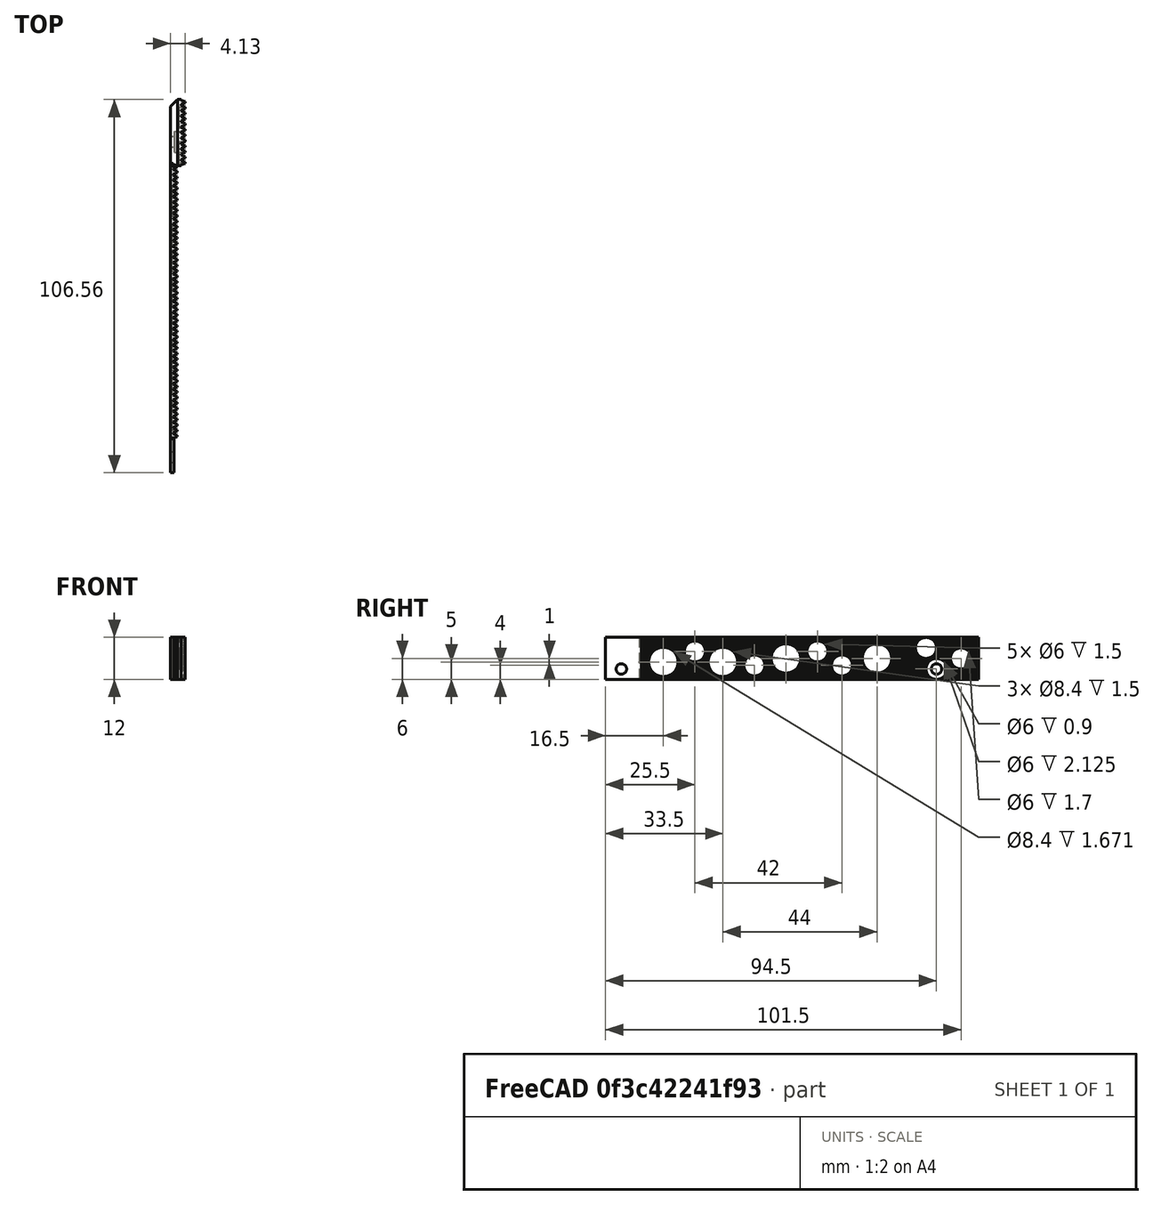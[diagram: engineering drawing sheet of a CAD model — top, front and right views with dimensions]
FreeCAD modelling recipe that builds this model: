
FCSTD DOCUMENT  (FreeCAD 0.19R24276 (Git))
Label: Grip_zubacka_005
License: All rights reserved
LicenseURL: http://en.wikipedia.org/wiki/All_rights_reserved
objects: Part::Cylinder×28, Part::Compound×7, Part::Cut×6, Part::Box×4, Part::FeaturePython×2, Part::Chamfer×1
note: 48 computed .brp shape members not serialized (recipe doc carries the construction recipe); baked Part::Feature solids carry a one-line shape summary decoded from their .brp

FEATURE [Part::FeaturePython] involuterack002  # WARN: FeaturePython — macro-defined, semantics opaque (R4)
  AttacherType = Attacher::AttachEngine3D
  Placement = pos=(23,6,-2) rot=(0,0,1;0rad)
  add_endings = true
  beta = 0
  clearance = 0.25
  double_helix = false
  head = 0
  height = 12
  module = 0.5
  pressure_angle = 20
  properties_from_tool = true
  simplified = false
  teeth = 50
  thickness = 0.8
  transverse_pitch = 1.5708
  version = 0.0.3
FEATURE [Part::FeaturePython] involuterack003  # WARN: FeaturePython — macro-defined, semantics opaque (R4)
  AttacherType = Attacher::AttachEngine3D
  Placement = pos=(25,81,-2) rot=(0,0,1;0rad)
  add_endings = true
  beta = 0
  clearance = 0.25
  double_helix = false
  head = 0
  height = 12
  module = 0.5
  pressure_angle = 20
  properties_from_tool = true
  simplified = false
  teeth = 12
  thickness = 1
  transverse_pitch = 1.5708
  version = 0.0.3
FEATURE [Part::Cylinder] Cylinder3127  label="Válec3097"
  Angle = 360
  AttacherType = Attacher::AttachEngine3D
  Height = 4
  Placement = pos=(1,14,-0.1) rot=(0,0,1;0rad)
  Radius = 1.5
FEATURE [Part::Box] Box1136  label="Krychle1135"
  AttacherType = Attacher::AttachEngine3D
  Height = 12
  Length = 1
  Placement = pos=(21.4,-4.5,-2) rot=(0,0,1;0rad)
  Width = 10
FEATURE [Part::Box] Box1133  label="Krychle1132"
  AttacherType = Attacher::AttachEngine3D
  Height = 2
  Length = 6
  Placement = pos=(-2,11,4) rot=(0,0,1;0rad)
  Width = 6
FEATURE [Part::Cylinder] Cylinder3125  label="Válec3095"
  Angle = 360
  AttacherType = Attacher::AttachEngine3D
  Height = 12
  Placement = pos=(1,14,6) rot=(0,0,1;0rad)
  Radius = 1.5
FEATURE [Part::Cylinder] Cylinder3128  label="Válec3098"
  Angle = 360
  AttacherType = Attacher::AttachEngine3D
  Height = 3
  Placement = pos=(1,14,6) rot=(0,0,1;0rad)
  Radius = 3
FEATURE [Part::Compound] Compound1376
  Links = -> [Cylinder3128]
  Placement = pos=(16.5,73,2) rot=(0,1,0;1.5708rad)
FEATURE [Part::Cut] Cut1266
  Base = -> involuterack003
  Placement = pos=(0.2,3,0) rot=(0,0,1;0rad)
  Tool = -> Compound1376
FEATURE [Part::Box] Box1134  label="Krychle1133"
  AttacherType = Attacher::AttachEngine3D
  Height = 12
  Length = 2
  Placement = pos=(21.4,80,-2) rot=(0,0,1;0rad)
  Width = 19
FEATURE [Part::Cylinder] Cylinder3123  label="Válec3093"
  Angle = 360
  AttacherType = Attacher::AttachEngine3D
  Height = 12
  Placement = pos=(1,14,6) rot=(0,0,1;0rad)
  Radius = 1.5
FEATURE [Part::Cylinder] Cylinder3124  label="Válec3094"
  Angle = 360
  AttacherType = Attacher::AttachEngine3D
  Height = 3
  Placement = pos=(1,14,6) rot=(0,0,1;0rad)
  Radius = 3
FEATURE [Part::Compound] Compound1375
  Links = -> [Cylinder3124]
  Placement = pos=(16.5,73,2) rot=(0,1,0;1.5708rad)
FEATURE [Part::Cylinder] Cylinder3126  label="Válec3096"
  Angle = 360
  AttacherType = Attacher::AttachEngine3D
  Height = 4
  Placement = pos=(1,14,-0.1) rot=(0,0,1;0rad)
  Radius = 1.5
FEATURE [Part::Compound] Compound1373
  Links = -> [Box1133,Cylinder3123,Cylinder3126]
  Placement = pos=(6,73,2) rot=(0,1,0;1.5708rad)
FEATURE [Part::Box] Box1135  label="Krychle1134"
  AttacherType = Attacher::AttachEngine3D
  Height = 2
  Length = 6
  Placement = pos=(-2,11,4) rot=(0,0,1;0rad)
  Width = 6
FEATURE [Part::Compound] Compound1374
  Links = -> [Box1135,Cylinder3125,Cylinder3127]
  Placement = pos=(6,-14,2) rot=(0,1,0;1.5708rad)
FEATURE [Part::Cut] Cut1267
  Base = -> Box1136
  Placement = pos=(0.2,0,0) rot=(0,0,1;0rad)
  Tool = -> Compound1374
FEATURE [Part::Cut] Cut1268
  Base = -> Box1134
  Tool = -> Compound1373
FEATURE [Part::Cut] Cut1269
  Base = -> Cut1268
  Tool = -> Compound1375
FEATURE [Part::Chamfer] Chamfer182
  Base = -> Cut1269
  Edges = 1 edges r=1.9: [Edge4]
  Placement = pos=(0.2,3,0) rot=(0,0,1;0rad)
FEATURE [Part::Cylinder] Cylinder  label="Válec"
  Angle = 360
  AttacherType = Attacher::AttachEngine3D
  Height = 10
  Placement = pos=(23,12,3) rot=(0,1,0;1.5708rad)
  Radius = 4.2
FEATURE [Part::Cylinder] Cylinder3129  label="Válec3099"
  Angle = 360
  AttacherType = Attacher::AttachEngine3D
  Height = 10
  Placement = pos=(23,38,2) rot=(0,1,0;1.5708rad)
  Radius = 3
FEATURE [Part::Cylinder] Cylinder3130  label="Válec3100"
  Angle = 360
  AttacherType = Attacher::AttachEngine3D
  Height = 10
  Placement = pos=(23,21,6) rot=(0,1,0;1.5708rad)
  Radius = 3
FEATURE [Part::Cylinder] Cylinder3131  label="Válec3101"
  Angle = 360
  AttacherType = Attacher::AttachEngine3D
  Height = 10
  Placement = pos=(23,47,4) rot=(0,1,0;1.5708rad)
  Radius = 4.2
FEATURE [Part::Cylinder] Cylinder3132  label="Válec3102"
  Angle = 360
  AttacherType = Attacher::AttachEngine3D
  Height = 10
  Placement = pos=(23,29,3) rot=(0,1,0;1.5708rad)
  Radius = 4.2
FEATURE [Part::Cylinder] Cylinder3133  label="Válec3103"
  Angle = 360
  AttacherType = Attacher::AttachEngine3D
  Height = 10
  Placement = pos=(23,56,6) rot=(0,1,0;1.5708rad)
  Radius = 3
FEATURE [Part::Cylinder] Cylinder3134  label="Válec3104"
  Angle = 360
  AttacherType = Attacher::AttachEngine3D
  Height = 10
  Placement = pos=(24,87,7) rot=(0,1,0;1.5708rad)
  Radius = 3
FEATURE [Part::Cylinder] Cylinder3135  label="Válec3105"
  Angle = 360
  AttacherType = Attacher::AttachEngine3D
  Height = 10
  Placement = pos=(23,73,4) rot=(0,1,0;1.5708rad)
  Radius = 4.2
FEATURE [Part::Cylinder] Cylinder3136  label="Válec3106"
  Angle = 360
  AttacherType = Attacher::AttachEngine3D
  Height = 10
  Placement = pos=(23,63,2) rot=(0,1,0;1.5708rad)
  Radius = 3
FEATURE [Part::Cylinder] Cylinder3137  label="Válec3107"
  Angle = 360
  AttacherType = Attacher::AttachEngine3D
  Height = 10
  Placement = pos=(23,63,2) rot=(0,1,0;1.5708rad)
  Radius = 3
FEATURE [Part::Cylinder] Cylinder3138  label="Válec3108"
  Angle = 360
  AttacherType = Attacher::AttachEngine3D
  Height = 10
  Placement = pos=(24,97,4) rot=(0,1,0;1.5708rad)
  Radius = 3
FEATURE [Part::Compound] Compound
  Links = -> [Cylinder,Cylinder3129,Cylinder3130,Cylinder3131,Cylinder3132,Cylinder3133,Cylinder3134,Cylinder3135,Cylinder3136,Cylinder3137,Cylinder3138]
  Placement = pos=(-1,0,0) rot=(0,0,1;0rad)
FEATURE [Part::Cylinder] Cylinder3139  label="Válec3109"
  Angle = 360
  AttacherType = Attacher::AttachEngine3D
  Height = 10
  Placement = pos=(23,12,3) rot=(0,1,0;1.5708rad)
  Radius = 4.2
FEATURE [Part::Cylinder] Cylinder3140  label="Válec3110"
  Angle = 360
  AttacherType = Attacher::AttachEngine3D
  Height = 10
  Placement = pos=(23,29,3) rot=(0,1,0;1.5708rad)
  Radius = 4.2
FEATURE [Part::Cylinder] Cylinder3141  label="Válec3111"
  Angle = 360
  AttacherType = Attacher::AttachEngine3D
  Height = 10
  Placement = pos=(24,87,7) rot=(0,1,0;1.5708rad)
  Radius = 3
FEATURE [Part::Cylinder] Cylinder3142  label="Válec3112"
  Angle = 360
  AttacherType = Attacher::AttachEngine3D
  Height = 10
  Placement = pos=(23,63,2) rot=(0,1,0;1.5708rad)
  Radius = 3
FEATURE [Part::Cylinder] Cylinder3143  label="Válec3113"
  Angle = 360
  AttacherType = Attacher::AttachEngine3D
  Height = 10
  Placement = pos=(23,38,2) rot=(0,1,0;1.5708rad)
  Radius = 3
FEATURE [Part::Cylinder] Cylinder3144  label="Válec3114"
  Angle = 360
  AttacherType = Attacher::AttachEngine3D
  Height = 10
  Placement = pos=(23,21,6) rot=(0,1,0;1.5708rad)
  Radius = 3
FEATURE [Part::Cylinder] Cylinder3145  label="Válec3115"
  Angle = 360
  AttacherType = Attacher::AttachEngine3D
  Height = 10
  Placement = pos=(23,56,6) rot=(0,1,0;1.5708rad)
  Radius = 3
FEATURE [Part::Cylinder] Cylinder3146  label="Válec3116"
  Angle = 360
  AttacherType = Attacher::AttachEngine3D
  Height = 10
  Placement = pos=(23,73,4) rot=(0,1,0;1.5708rad)
  Radius = 4.2
FEATURE [Part::Cylinder] Cylinder3147  label="Válec3117"
  Angle = 360
  AttacherType = Attacher::AttachEngine3D
  Height = 10
  Placement = pos=(23,63,2) rot=(0,1,0;1.5708rad)
  Radius = 3
FEATURE [Part::Cylinder] Cylinder3148  label="Válec3118"
  Angle = 360
  AttacherType = Attacher::AttachEngine3D
  Height = 10
  Placement = pos=(23,47,4) rot=(0,1,0;1.5708rad)
  Radius = 4.2
FEATURE [Part::Cylinder] Cylinder3149  label="Válec3119"
  Angle = 360
  AttacherType = Attacher::AttachEngine3D
  Height = 10
  Placement = pos=(24,97,4) rot=(0,1,0;1.5708rad)
  Radius = 3
FEATURE [Part::Compound] Compound1377
  Links = -> [Cylinder3139,Cylinder3143,Cylinder3144,Cylinder3148,Cylinder3140,Cylinder3145,Cylinder3141,Cylinder3146,Cylinder3142,Cylinder3147,Cylinder3149]
FEATURE [Part::Cut] Cut
  Base = -> Cut1266
  Tool = -> Compound1377
FEATURE [Part::Cut] Cut1270
  Base = -> involuterack002
  Tool = -> Compound
FEATURE [Part::Compound] Compound1378  label="Grip_finger-toothed-belt"
  Links = -> [Cut1267,Chamfer182,Cut,Cut1270]
